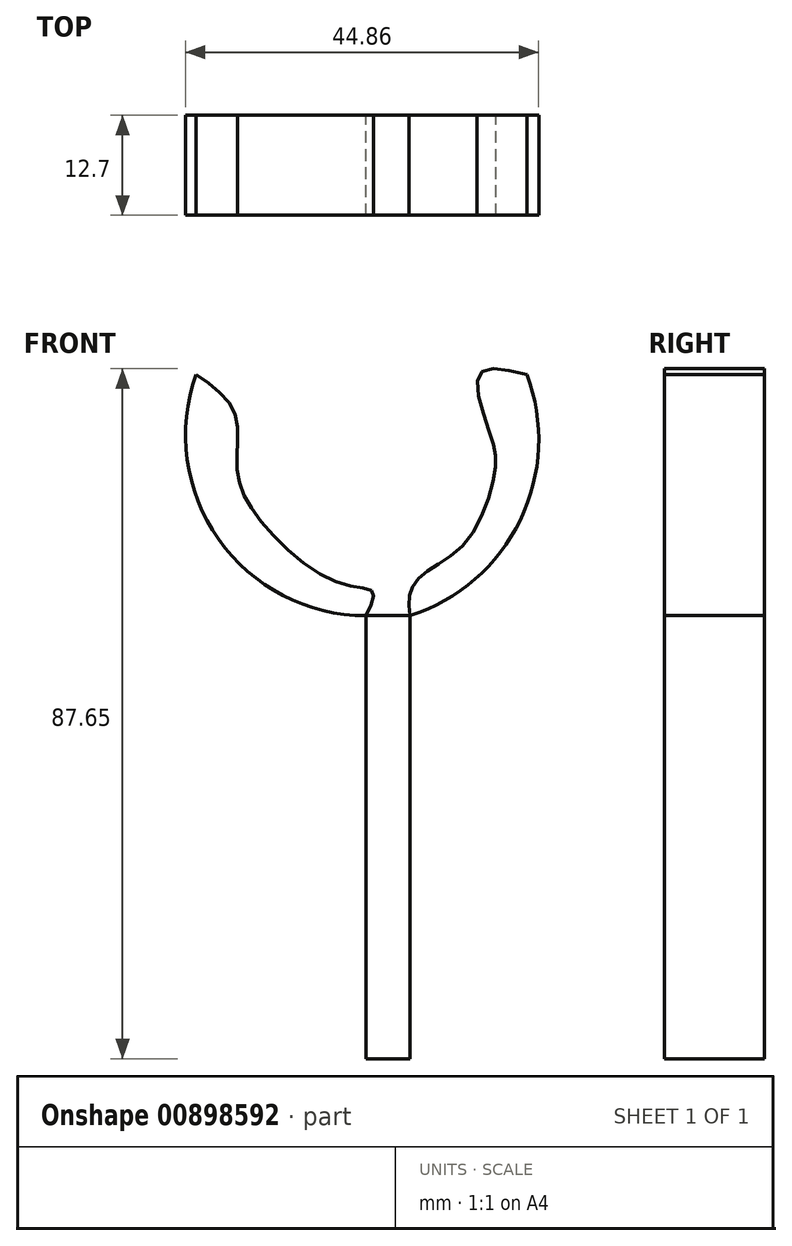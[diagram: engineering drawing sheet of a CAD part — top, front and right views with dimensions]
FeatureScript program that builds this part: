
annotation { "Feature Type Name" : "Feature", "Feature Type Description" : "" }
export const myFeature = defineFeature(function(context is Context, id is Id, definition is map)
    precondition{}
    {
        {
            var Q0;
            Q0=qCreatedBy(makeId("Front.planeOp"),FACE);
            var sketch = newSketch(context, id + "F0", { "sketchPlane" : qUnion([Q0])});
            skLineSegment(sketch, "E0.bottom", {"start": v(-5.61, 0) * mm, "end": v(0, 0) * mm});
            skLineSegment(sketch, "E0.top", {"start": v(-5.61, -56.27) * mm, "end": v(0, -56.27) * mm});
            skLineSegment(sketch, "E0.left", {"start": v(-5.61, 0) * mm, "end": v(-5.61, -56.27) * mm});
            skLineSegment(sketch, "E0.right", {"start": v(0, 0) * mm, "end": v(0, -56.27) * mm});
            skArc(sketch, "E1", {"start": v(-27.2, 30.65) * mm, "mid": v(-24.36, 9.73) * mm, "end": v(-5.61, 0) * mm});
            skArc(sketch, "E2", {"start": v(0, 0) * mm, "mid": v(13.98, 12.15) * mm, "end": v(14.82, 30.65) * mm});
            skFitSpline(sketch, "E3", {"points": [v(-27.2, 30.65) * mm, v(-22.3, 25.76) * mm, v(-22.02, 18.85) * mm, v(-19.14, 12.23) * mm, v(-9.07, 4.17) * mm, v(-4.75, 3.02) * mm, v(-5.61, 0) * mm], "startDerivative": vector(36.51, -25.23) * mm, "endDerivative": vector(-16.04, -31.88) * mm});
            skFitSpline(sketch, "E4", {"points": [v(14.82, 30.65) * mm, v(8.78, 30.65) * mm, v(10.22, 22.93) * mm, v(10.8, 18.56) * mm, v(7.34, 9.64) * mm, v(2.16, 5.61) * mm, v(0, 3.02) * mm, v(0, 0) * mm], "startDerivative": vector(-53.3, 12.8) * mm, "endDerivative": vector(4.09, -30) * mm});
            skSolve(sketch);
        }
        {
            var Q0;
            Q0 = qSketchRegion(id + "F0", true);
            extrude(context, id + "F1", {"entities" : qUnion([Q0]), "depth" : 12.7 * mm, "offsetDistance" : 25.4 * mm});
        }
    });
